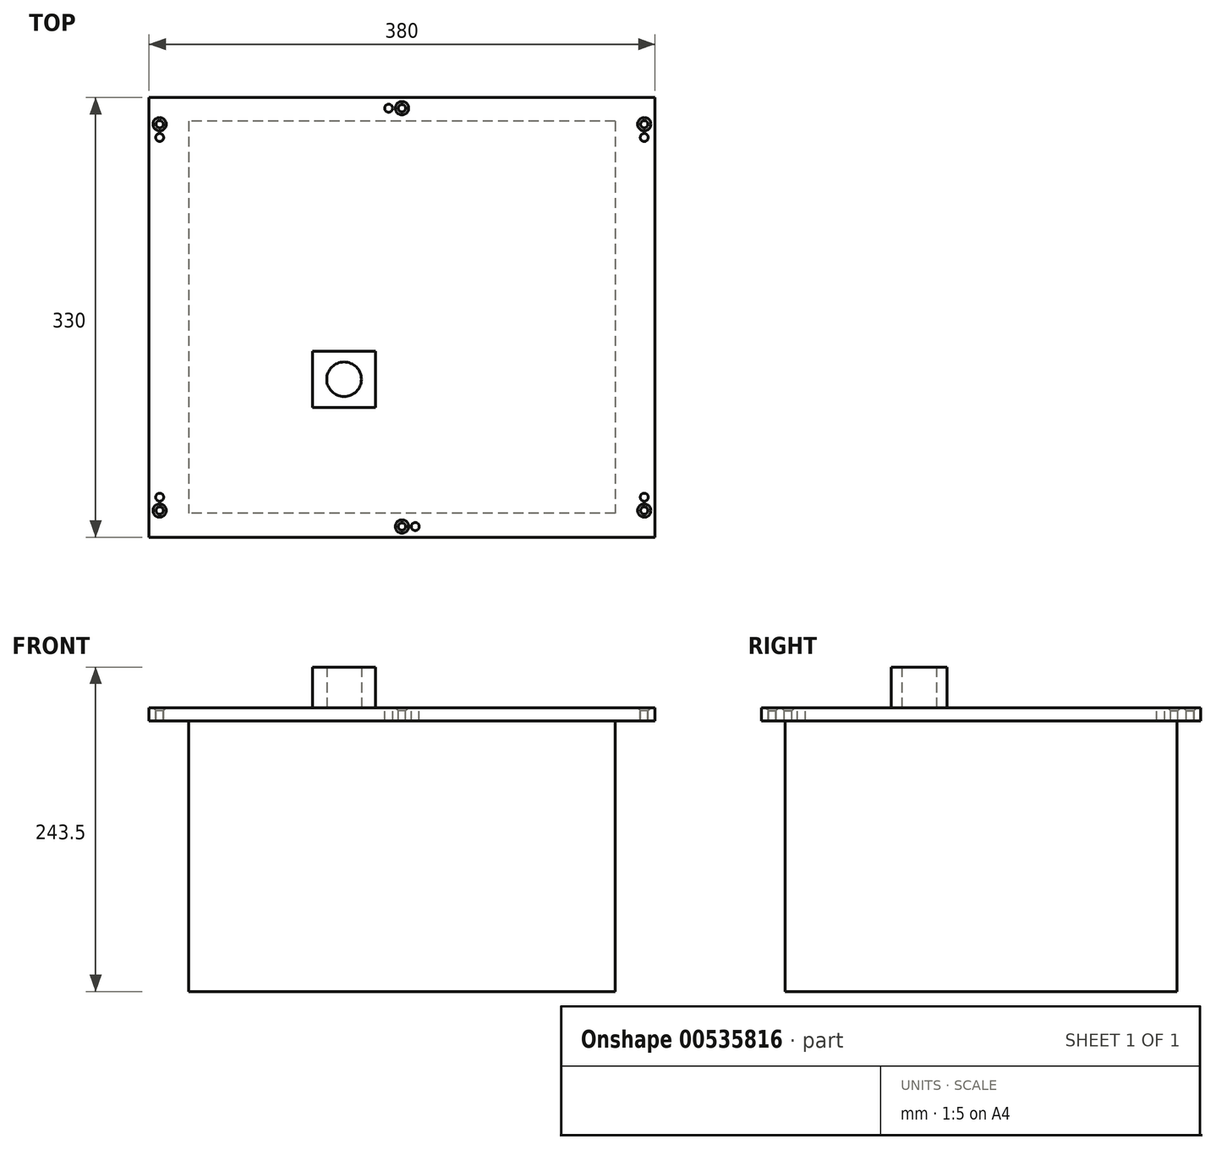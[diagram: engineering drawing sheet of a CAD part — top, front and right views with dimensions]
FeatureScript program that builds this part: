
annotation { "Feature Type Name" : "Feature", "Feature Type Description" : "" }
export const myFeature = defineFeature(function(context is Context, id is Id, definition is map)
    precondition{}
    {
        {
            var Q0;
            Q0=qCreatedBy(makeId("Top.planeOp"),FACE);
            var sketch = newSketch(context, id + "F0", { "sketchPlane" : qUnion([Q0])});
            skLineSegment(sketch, "E0.bottom", {"start": v(190, -165) * mm, "end": v(-190, -165) * mm});
            skLineSegment(sketch, "E0.top", {"start": v(190, 165) * mm, "end": v(-190, 165) * mm});
            skLineSegment(sketch, "E0.left", {"start": v(190, -165) * mm, "end": v(190, 165) * mm});
            skLineSegment(sketch, "E0.right", {"start": v(-190, -165) * mm, "end": v(-190, 165) * mm});
            skPoint(sketch, "E0.middle", {"position": v(0, 0) * mm});
            skSolve(sketch);
        }
        {
            var Q0;
            Q0=qSketchRegion(id+"F0",true);
            extrude(context, id + "F1", {"entities" : qUnion([Q0]), "depth" : 10 * mm});
        }
        {
            var Q0;
            Q0=makeQuery(id+"F1.opExtrude","CAP_FACE",FACE,{"disambiguationData":[OSD([sQuery(id+"F0.wireOp",EDGE,"E0.bottom"),sQuery(id+"F0.wireOp",EDGE,"E0.top"),sQuery(id+"F0.wireOp",EDGE,"E0.left"),sQuery(id+"F0.wireOp",EDGE,"E0.right")])],"isStart":true});
            var sketch = newSketch(context, id + "F2", { "sketchPlane" : qUnion([Q0])});
            skLineSegment(sketch, "E1.bottom", {"start": v(160.15, -147.15) * mm, "end": v(-160.15, -147.15) * mm});
            skLineSegment(sketch, "E1.top", {"start": v(160.15, 147.15) * mm, "end": v(-160.15, 147.15) * mm});
            skLineSegment(sketch, "E1.left", {"start": v(160.15, -147.15) * mm, "end": v(160.15, 147.15) * mm});
            skLineSegment(sketch, "E1.right", {"start": v(-160.15, -147.15) * mm, "end": v(-160.15, 147.15) * mm});
            skPoint(sketch, "E1.middle", {"position": v(0, 0) * mm});
            skSolve(sketch);
        }
        {
            var Q0;
            Q0=qSketchRegion(id+"F2",true);
            extrude(context, id + "F3", {"entities" : qUnion([Q0]), "operationType" : NewBodyOperationType.ADD, "depth" : 203 * mm});
        }
        {
            var Q0;
            Q0=makeQuery(id+"F1.opExtrude","CAP_FACE",FACE,{"disambiguationData":[OSD([sQuery(id+"F0.wireOp",EDGE,"E0.bottom"),sQuery(id+"F0.wireOp",EDGE,"E0.top"),sQuery(id+"F0.wireOp",EDGE,"E0.left"),sQuery(id+"F0.wireOp",EDGE,"E0.right")])],"isStart":false});
            var sketch = newSketch(context, id + "F4", { "sketchPlane" : qUnion([Q0])});
            skLineSegment(sketch, "E2.bottom", {"start": v(-19.75, -67.5) * mm, "end": v(-67.25, -67.5) * mm});
            skLineSegment(sketch, "E2.top", {"start": v(-19.75, -25.5) * mm, "end": v(-67.25, -25.5) * mm});
            skLineSegment(sketch, "E2.left", {"start": v(-19.75, -67.5) * mm, "end": v(-19.75, -25.5) * mm});
            skLineSegment(sketch, "E2.right", {"start": v(-67.25, -67.5) * mm, "end": v(-67.25, -25.5) * mm});
            skPoint(sketch, "E2.middle", {"position": v(-43.5, -46.5) * mm});
            skCircle(sketch, "E3", {"center": v(-43.5, -46.5) * mm, "radius": 13 * mm});
            skSolve(sketch);
        }
        {
            var Q0;
            Q0=qSketchRegion(id+"F4",true);
            extrude(context, id + "F5", {"entities" : qUnion([Q0]), "operationType" : NewBodyOperationType.ADD, "depth" : 30.5 * mm});
        }
        {
            var Q0;
            {var subQ0=sQuery(id+"F0.wireOp",EDGE,"E0.left");var subQ1=sQuery(id+"F0.wireOp",EDGE,"E0.top");var subQ2=sQuery(id+"F0.wireOp",EDGE,"E0.right");var subQ3=sQuery(id+"F0.wireOp",EDGE,"E0.bottom");Q0=makeQuery(id+"F5.boolean.opBoolean","SPLIT",FACE,{"disambiguationData":[TD([makeQuery(id+"F1.opExtrude","SWEPT_FACE",FACE,{"disambiguationData":[OSD([subQ3])]})])],"derivedFrom":makeQuery(id+"F1.opExtrude","CAP_FACE",FACE,{"disambiguationData":[OSD([subQ3,subQ1,subQ0,subQ2])],"isStart":false})});}
            var sketch = newSketch(context, id + "F6", { "sketchPlane" : qUnion([Q0])});
            skPoint(sketch, "E4", {"position": v(0, 157) * mm});
            skPoint(sketch, "E5", {"position": v(0, -157) * mm});
            skPoint(sketch, "E6", {"position": v(-182, 145) * mm});
            skPoint(sketch, "E7", {"position": v(-182, -145) * mm});
            skPoint(sketch, "E8", {"position": v(-182, 135) * mm});
            skPoint(sketch, "E9", {"position": v(-182, -135) * mm});
            skPoint(sketch, "E10.MirrorP", {"position": v(182, 145) * mm});
            skPoint(sketch, "E11.MirrorP", {"position": v(182, -145) * mm});
            skPoint(sketch, "E12.MirrorP", {"position": v(182, 135) * mm});
            skPoint(sketch, "E13.MirrorP", {"position": v(182, -135) * mm});
            skPoint(sketch, "E14", {"position": v(-10, 157) * mm});
            skPoint(sketch, "E15", {"position": v(10, -157) * mm});
            skSolve(sketch);
        }
        {
            var Q0;
            Q0=sQuery(id+"F6.wireOp",VERTEX,"E8");
            var Q1;
            Q1=sQuery(id+"F6.wireOp",VERTEX,"E9");
            var Q2;
            Q2=sQuery(id+"F6.wireOp",VERTEX,"E12.MirrorP");
            var Q3;
            Q3=sQuery(id+"F6.wireOp",VERTEX,"E13.MirrorP");
            var Q4;
            Q4=sQuery(id+"F6.wireOp",VERTEX,"E15");
            var Q5;
            Q5=sQuery(id+"F6.wireOp",VERTEX,"E14");
            var Q6;
            Q6=makeQuery(id+"F1.opExtrude","SWEPT_BODY",BODY,{"disambiguationData":[OSD([sQuery(id+"F0.wireOp",EDGE,"E0.bottom"),sQuery(id+"F0.wireOp",EDGE,"E0.top"),sQuery(id+"F0.wireOp",EDGE,"E0.left"),sQuery(id+"F0.wireOp",EDGE,"E0.right")])]});
            hole(context, id + "F7", {"style" : HoleStyle.SIMPLE, "endStyle" : HoleEndStyle.BLIND, "holeDiameter" : 6 * mm, "holeDepth" : 10 * mm, "tappedDepth" : 12 * mm, "tapClearance" : 3, "locations" : qUnion([Q0, Q1, Q2, Q3, Q4, Q5]), "scope" : qUnion([Q6])});
        }
        {
            var Q0;
            Q0=sQuery(id+"F6.wireOp",VERTEX,"E6");
            var Q1;
            Q1=sQuery(id+"F6.wireOp",VERTEX,"E10.MirrorP");
            var Q2;
            Q2=sQuery(id+"F6.wireOp",VERTEX,"E7");
            var Q3;
            Q3=sQuery(id+"F6.wireOp",VERTEX,"E11.MirrorP");
            var Q4;
            Q4=sQuery(id+"F6.wireOp",VERTEX,"E5");
            var Q5;
            Q5=sQuery(id+"F6.wireOp",VERTEX,"E4");
            var Q6;
            Q6=makeQuery(id+"F1.opExtrude","SWEPT_BODY",BODY,{"disambiguationData":[OSD([sQuery(id+"F0.wireOp",EDGE,"E0.bottom"),sQuery(id+"F0.wireOp",EDGE,"E0.top"),sQuery(id+"F0.wireOp",EDGE,"E0.left"),sQuery(id+"F0.wireOp",EDGE,"E0.right")])]});
            hole(context, id + "F8", {"style" : HoleStyle.C_SINK, "endStyle" : HoleEndStyle.BLIND, "holeDiameter" : 5.5 * mm, "cSinkDiameter" : 10 * mm, "cSinkAngle" : 90 * degree, "holeDepth" : 10 * mm, "tappedDepth" : 12 * mm, "tapClearance" : 3, "locations" : qUnion([Q0, Q1, Q2, Q3, Q4, Q5]), "scope" : qUnion([Q6])});
        }
    });
